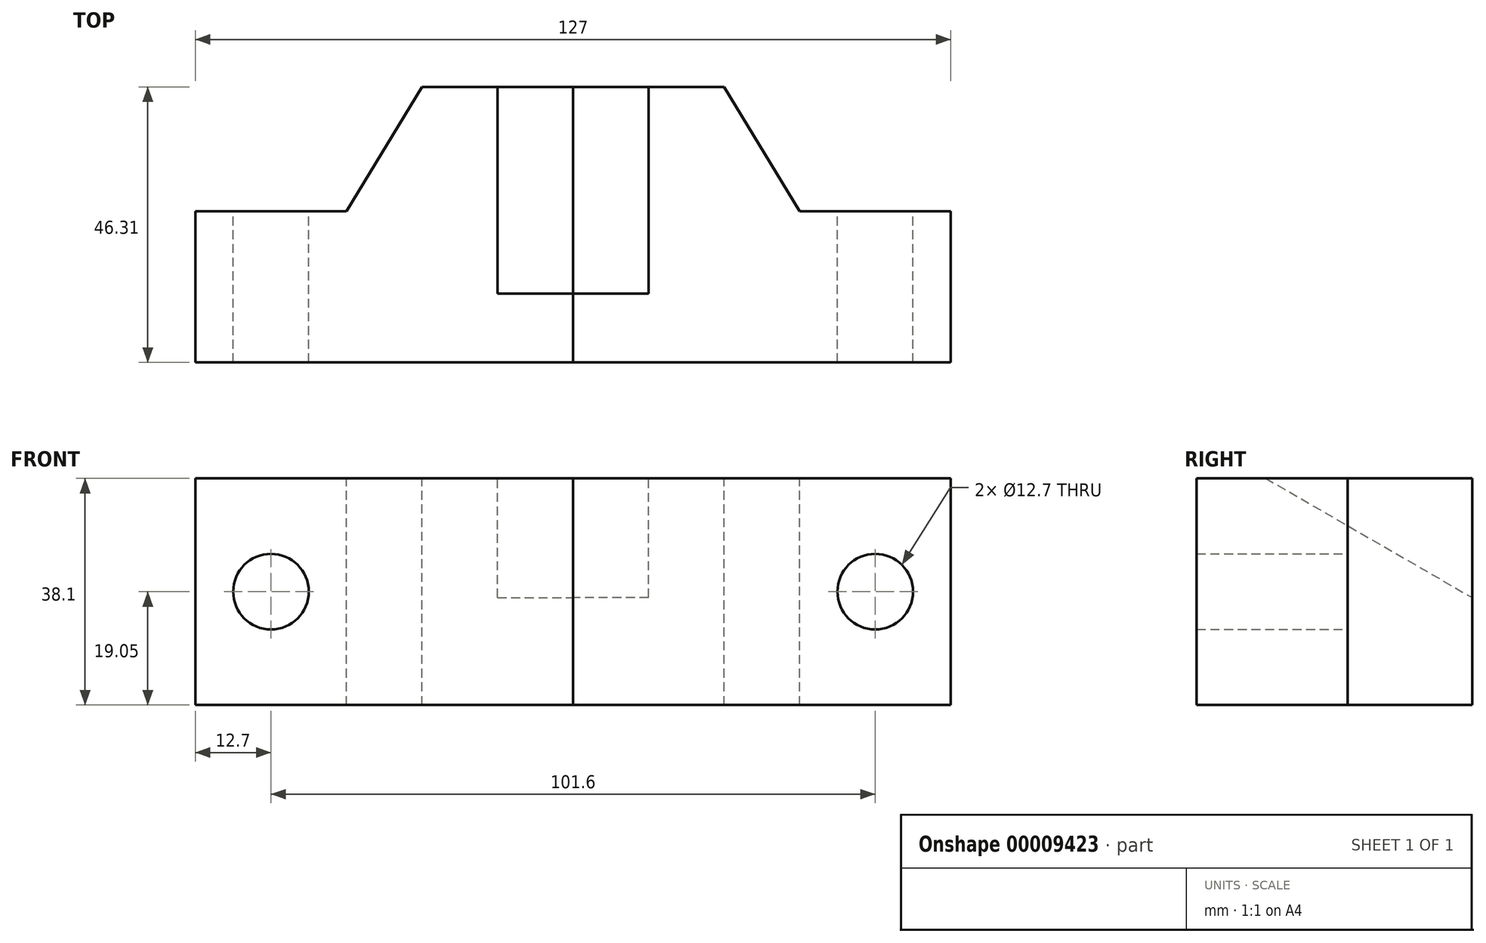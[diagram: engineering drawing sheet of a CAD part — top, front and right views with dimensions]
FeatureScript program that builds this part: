
annotation { "Feature Type Name" : "Feature", "Feature Type Description" : "" }
export const myFeature = defineFeature(function(context is Context, id is Id, definition is map)
    precondition{}
    {
        {
            var Q0;
            Q0=qCreatedBy(makeId("Top.planeOp"),FACE);
            var sketch = newSketch(context, id + "F0", { "sketchPlane" : qUnion([Q0])});
            skLineSegment(sketch, "E0", {"start": v(0, -11.59) * mm, "end": v(0, 34.72) * mm});
            skLineSegment(sketch, "E1", {"start": v(0, 34.72) * mm, "end": v(-25.4, 34.72) * mm});
            skLineSegment(sketch, "E2", {"start": v(-25.4, 34.72) * mm, "end": v(-38.1, 13.81) * mm});
            skLineSegment(sketch, "E3", {"start": v(-38.1, 13.81) * mm, "end": v(-63.5, 13.81) * mm});
            skLineSegment(sketch, "E4", {"start": v(-63.5, 13.81) * mm, "end": v(-63.5, -11.59) * mm});
            skLineSegment(sketch, "E5", {"start": v(-63.5, -11.59) * mm, "end": v(0, -11.59) * mm});
            skLineSegment(sketch, "E6", {"start": v(0, 1.11) * mm, "end": v(-12.7, 1.11) * mm});
            skLineSegment(sketch, "E7", {"start": v(-12.7, 1.11) * mm, "end": v(-12.7, 34.72) * mm});
            skLineSegment(sketch, "E8", {"start": v(-50.8, 13.81) * mm, "end": v(-50.8, -11.59) * mm, "construction": true});
            skSolve(sketch);
        }
        {
            var Q0;
            {var subQ2=sQuery(id+"F0.wireOp",EDGE,"E2");Q0=makeQuery(id+"F0.imprint","IMPRINT",FACE,{"disambiguationData":[TD([[makeQuery(id+"F0.imprint","IMPRINT",EDGE,{"derivedFrom":subQ2}),1.0]])]});}
            var Q1;
            {var subQ1=sQuery(id+"F0.wireOp",EDGE,"E6");Q1=makeQuery(id+"F0.imprint","IMPRINT",FACE,{"disambiguationData":[TD([[makeQuery(id+"F0.imprint","IMPRINT",EDGE,{"derivedFrom":subQ1}),-1.0]])]});}
            extrude(context, id + "F1", {"entities" : qUnion([Q0, Q1]), "oppositeDirection" : true, "depth" : 38.1 * mm});
        }
        {
            var Q0;
            Q0=makeQuery(id+"F1.opExtrude","SWEPT_FACE",FACE,{"disambiguationData":[OSD([sQuery(id+"F0.wireOp",EDGE,"E0")])]});
            var sketch = newSketch(context, id + "F2", { "sketchPlane" : qUnion([Q0])});
            skLineSegment(sketch, "E9", {"start": v(0, 0) * mm, "end": v(34.72, -20.05) * mm});
            skSolve(sketch);
        }
        {
            var Q0;
            {var subQ2=sQuery(id+"F2.wireOp",EDGE,"E9");Q0=makeQuery(id+"F2.imprint","IMPRINT",FACE,{"disambiguationData":[TD([[makeQuery(id+"F2.imprint","IMPRINT",EDGE,{"derivedFrom":subQ2}),1.0]])]});}
            extrude(context, id + "F3", {"entities" : qUnion([Q0]), "operationType" : NewBodyOperationType.REMOVE, "oppositeDirection" : true, "depth" : 12.7 * mm});
        }
        {
            var Q0;
            Q0=makeQuery(id+"F1.opExtrude","SWEPT_FACE",FACE,{"disambiguationData":[OSD([sQuery(id+"F0.wireOp",EDGE,"E3")])]});
            var sketch = newSketch(context, id + "F4", { "sketchPlane" : qUnion([Q0])});
            skLineSegment(sketch, "E10", {"start": v(50.8, 0) * mm, "end": v(50.8, -38.1) * mm, "construction": true});
            skCircle(sketch, "E11", {"center": v(50.8, -19.05) * mm, "radius": 6.35 * mm});
            skSolve(sketch);
        }
        {
            var Q0;
            Q0=makeQuery(id+"F4.imprint","IMPRINT",FACE,{"disambiguationData":[TD([[makeQuery(id+"F4.imprint","IMPRINT",EDGE,{"derivedFrom":sQuery(id+"F4.wireOp",EDGE,"E11")}),1.0]])]});
            extrude(context, id + "F5", {"entities" : qUnion([Q0]), "operationType" : NewBodyOperationType.REMOVE, "endBound" : BoundingType.THROUGH_ALL, "oppositeDirection" : true, "depth" : 25.4 * mm});
        }
        {
            var Q0;
            Q0=makeQuery(id+"F1.opExtrude","SWEPT_BODY",BODY,{"disambiguationData":[OSD([sQuery(id+"F0.wireOp",EDGE,"E0"),sQuery(id+"F0.wireOp",EDGE,"E1"),sQuery(id+"F0.wireOp",EDGE,"E2"),sQuery(id+"F0.wireOp",EDGE,"E3"),sQuery(id+"F0.wireOp",EDGE,"E4"),sQuery(id+"F0.wireOp",EDGE,"E5")])]});
            var Q1;
            Q1=qCreatedBy(makeId("Right.planeOp"),FACE);
            mirror(context, id + "F6", {"entities" : qUnion([Q0]), "mirrorPlane" : qUnion([Q1])});
        }
    });
